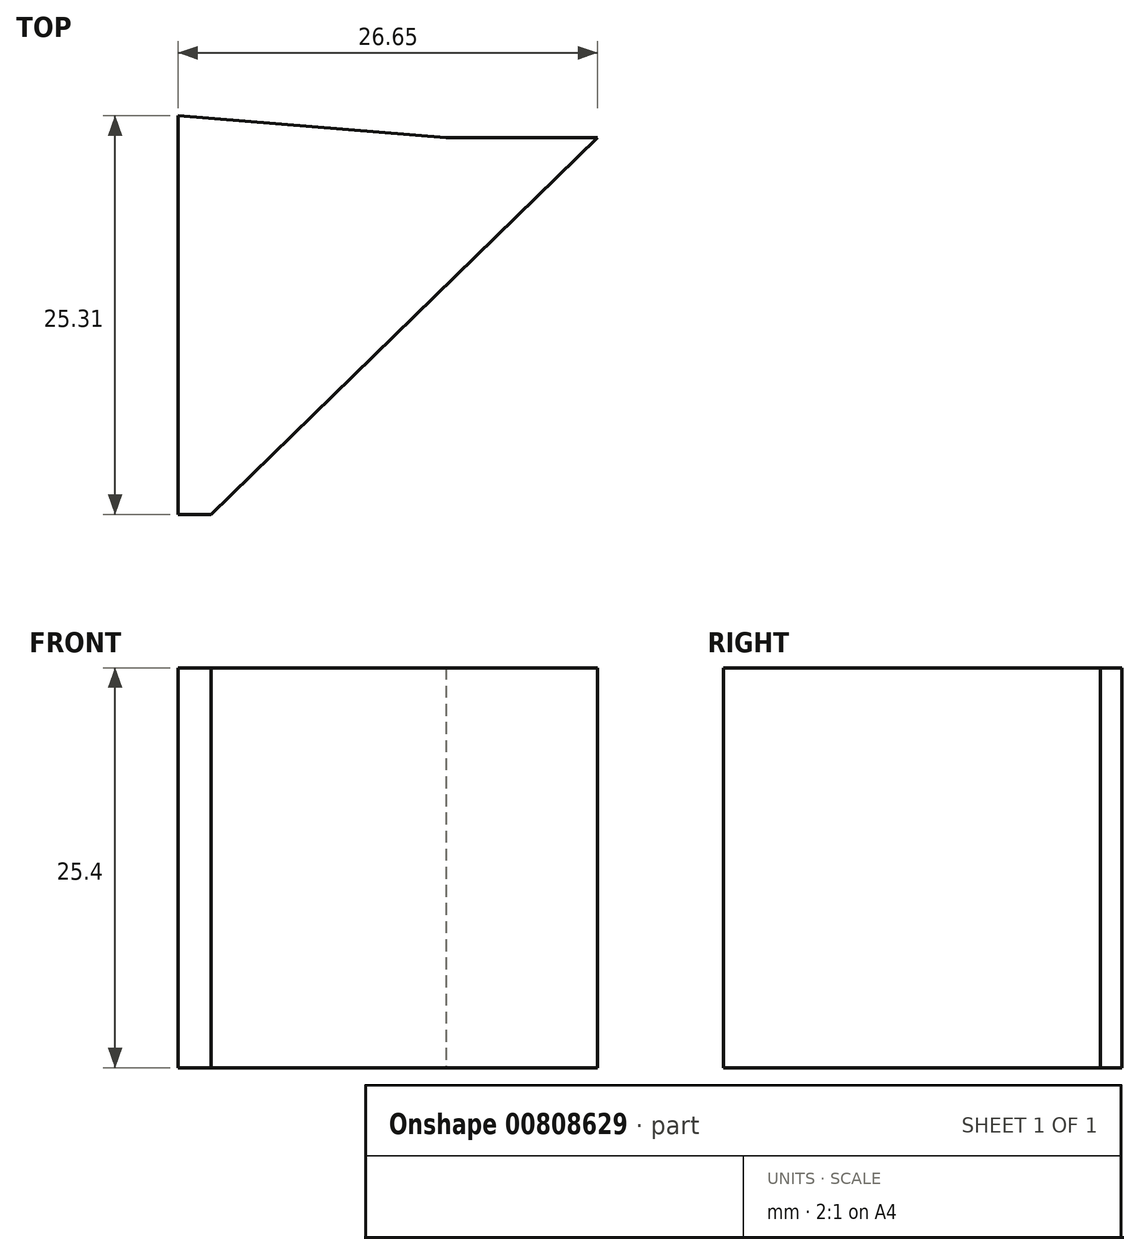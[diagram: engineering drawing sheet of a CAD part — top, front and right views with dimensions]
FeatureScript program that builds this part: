
annotation { "Feature Type Name" : "Feature", "Feature Type Description" : "" }
export const myFeature = defineFeature(function(context is Context, id is Id, definition is map)
    precondition{}
    {
        {
            var Q0;
            Q0=qCreatedBy(makeId("Top.planeOp"),FACE);
            var sketch = newSketch(context, id + "F0", { "sketchPlane" : qUnion([Q0])});
            skLineSegment(sketch, "E0", {"start": v(0, 0) * mm, "end": v(17.03, 23.93) * mm});
            skLineSegment(sketch, "E1", {"start": v(0, 25.3) * mm, "end": v(17.03, 23.93) * mm});
            skLineSegment(sketch, "E2", {"start": v(0, 25.3) * mm, "end": v(0, 0) * mm});
            skLineSegment(sketch, "E3", {"start": v(26.65, 23.93) * mm, "end": v(2.1, 0) * mm});
            skLineSegment(sketch, "E4", {"start": v(2.1, 0) * mm, "end": v(17.03, 23.93) * mm});
            skLineSegment(sketch, "E5", {"start": v(0, 0) * mm, "end": v(2.1, 0) * mm});
            skLineSegment(sketch, "E6", {"start": v(17.03, 23.93) * mm, "end": v(26.65, 23.93) * mm});
            skSolve(sketch);
        }
        {
            var Q0;
            Q0=makeQuery(id+"F0.imprint","IMPRINT",FACE,{"disambiguationData":[TD([[makeQuery(id+"F0.imprint","IMPRINT",EDGE,{"derivedFrom":sQuery(id+"F0.wireOp",EDGE,"E0")}),1.0]])]});
            var Q1;
            Q1=makeQuery(id+"F0.imprint","IMPRINT",FACE,{"disambiguationData":[TD([[makeQuery(id+"F0.imprint","IMPRINT",EDGE,{"derivedFrom":sQuery(id+"F0.wireOp",EDGE,"E0")}),-1.0]])]});
            var Q2;
            Q2=makeQuery(id+"F0.imprint","IMPRINT",FACE,{"disambiguationData":[TD([[makeQuery(id+"F0.imprint","IMPRINT",EDGE,{"derivedFrom":sQuery(id+"F0.wireOp",EDGE,"E3")}),-1.0]])]});
            extrude(context, id + "F1", {"entities" : qUnion([Q0, Q1, Q2]), "depth" : 25.4 * mm, "offsetDistance" : 25.4 * mm});
        }
    });
